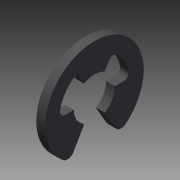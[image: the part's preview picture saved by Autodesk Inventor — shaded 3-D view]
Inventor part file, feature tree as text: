
AUTODESK INVENTOR PART (.ipt)
format: ipt  version: 2014 (Build 180170000, 170)  size: 127,488 bytes
history: native  units: in
note: dims shown in document units (in); Inventor stores cm internally (conversion verified against a paired STEP export)
features: other x7, extrude x1, sketch x1
ambient origin geometry x8: Origin, YZ Plane, XZ Plane, XY Plane, X Axis, Y Axis, Z Axis, Center Point
bodies: Solid1 (feature_tree)
feature tree (9):
  extrude  "Extrusion1"  [1 undecoded]
  other  "rr_XY"
  other  "rr_YZ"
  other  "rr_ZX"
  other  "rr_X"
  other  "rr_Y"
  other  "rr_Z"
  other  "rr_Center"
  sketch  "Sketch_1"  dims[d0=0.025in d1=0.0in]
note: 1 required parameter value undecoded (feature->parameter linkage not recoverable at this tier; creation-order binding heuristic only, values carry confidence <= 0.55)
